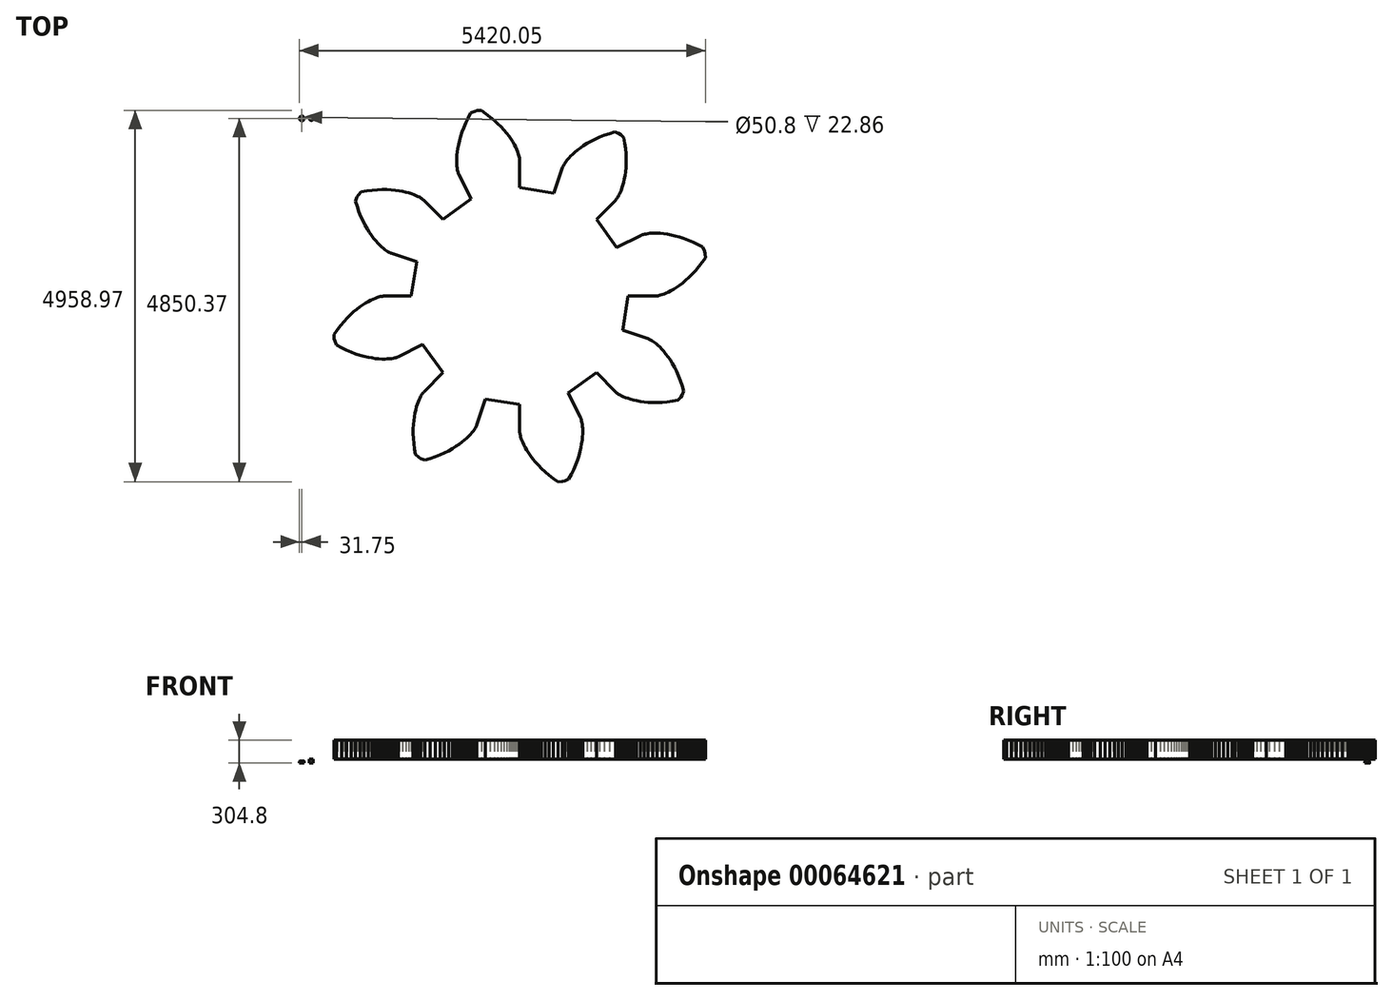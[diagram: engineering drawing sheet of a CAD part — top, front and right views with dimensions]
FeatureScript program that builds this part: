
annotation { "Feature Type Name" : "Feature", "Feature Type Description" : "" }
export const myFeature = defineFeature(function(context is Context, id is Id, definition is map)
    precondition{}
    {
        {
            var Q0;
            Q0=qCreatedBy(makeId("Top.planeOp"),FACE);
            var sketch = newSketch(context, id + "F0", { "sketchPlane" : qUnion([Q0])});
            skCircle(sketch, "E0", {"center": v(-25.4, 10.89) * mm, "radius": 25.4 * mm});
            skCircle(sketch, "E1", {"center": v(101.6, 10.89) * mm, "radius": 25.46 * mm});
            skCircle(sketch, "E2.0", {"center": v(-25.4, 10.89) * mm, "radius": 31.75 * mm});
            skSolve(sketch);
        }
        {
            var Q0;
            Q0=makeQuery(id+"F0.imprint","IMPRINT",FACE,{"disambiguationData":[TD([[makeQuery(id+"F0.imprint","IMPRINT",EDGE,{"derivedFrom":sQuery(id+"F0.wireOp",EDGE,"E0")}),-1.0]])]});
            extrude(context, id + "F1", {"entities" : qUnion([Q0]), "depth" : 25.4 * mm});
        }
        {
            var Q0;
            Q0=makeQuery(id+"F0.imprint","IMPRINT",FACE,{"disambiguationData":[TD([[makeQuery(id+"F0.imprint","IMPRINT",EDGE,{"derivedFrom":sQuery(id+"F0.wireOp",EDGE,"E1")}),1.0]])]});
            extrude(context, id + "F2", {"entities" : qUnion([Q0]), "depth" : 50.8 * mm});
        }
        {
            var Q0;
            Q0=makeQuery(id+"F1.opExtrude","CAP_EDGE",EDGE,{"disambiguationData":[OSD([sQuery(id+"F0.wireOp",EDGE,"E0")])],"isStart":false});
            fillet(context, id + "F3", {"entities" : qUnion([Q0]), "radius" : 2.54 * mm, "tangentPropagation" : true, "allowEdgeOverflow" : false});
        }
        {
            var Q0;
            Q0=makeQuery(id+"F1.opExtrude","CAP_EDGE",EDGE,{"disambiguationData":[OSD([sQuery(id+"F0.wireOp",EDGE,"E2.0")])],"isStart":false});
            chamfer(context, id + "F4", {"entities" : qUnion([Q0]), "width" : 5.08 * mm, "tangentPropagation" : true});
        }
        {
            var Q0;
            Q0=makeQuery(id+"F2.opExtrude","CAP_FACE",FACE,{"disambiguationData":[OSD([sQuery(id+"F0.wireOp",EDGE,"E1")])],"isStart":false});
            var sketch = newSketch(context, id + "F5", { "sketchPlane" : qUnion([Q0])});
            skLineSegment(sketch, "E3", {"start": v(4703.84, -2359.3) * mm, "end": v(4713.76, -2358.02) * mm});
            skLineSegment(sketch, "E4", {"start": v(4713.76, -2358.02) * mm, "end": v(4727, -2355.74) * mm});
            skLineSegment(sketch, "E5", {"start": v(4727, -2355.74) * mm, "end": v(4743.5, -2352.14) * mm});
            skLineSegment(sketch, "E6", {"start": v(4743.5, -2352.14) * mm, "end": v(4763.16, -2346.95) * mm});
            skLineSegment(sketch, "E7", {"start": v(4763.16, -2346.95) * mm, "end": v(4785.87, -2339.89) * mm});
            skLineSegment(sketch, "E8", {"start": v(4785.87, -2339.89) * mm, "end": v(4811.5, -2330.67) * mm});
            skLineSegment(sketch, "E9", {"start": v(4811.5, -2330.67) * mm, "end": v(4839.88, -2319.05) * mm});
            skLineSegment(sketch, "E10", {"start": v(4839.88, -2319.05) * mm, "end": v(4870.87, -2304.75) * mm});
            skLineSegment(sketch, "E11", {"start": v(4870.87, -2304.75) * mm, "end": v(4904.26, -2287.54) * mm});
            skLineSegment(sketch, "E12", {"start": v(4904.26, -2287.54) * mm, "end": v(4939.86, -2267.17) * mm});
            skLineSegment(sketch, "E13", {"start": v(4939.86, -2267.17) * mm, "end": v(4977.46, -2243.43) * mm});
            skLineSegment(sketch, "E14", {"start": v(4977.46, -2243.43) * mm, "end": v(5016.82, -2216.12) * mm});
            skLineSegment(sketch, "E15", {"start": v(5016.82, -2216.12) * mm, "end": v(5057.69, -2185.02) * mm});
            skLineSegment(sketch, "E16", {"start": v(5057.69, -2185.02) * mm, "end": v(5099.82, -2149.97) * mm});
            skLineSegment(sketch, "E17", {"start": v(5099.82, -2149.97) * mm, "end": v(5142.92, -2110.8) * mm});
            skLineSegment(sketch, "E18", {"start": v(5142.92, -2110.8) * mm, "end": v(5186.73, -2067.35) * mm});
            skLineSegment(sketch, "E19", {"start": v(5186.73, -2067.35) * mm, "end": v(5230.94, -2019.5) * mm});
            skLineSegment(sketch, "E20", {"start": v(5230.94, -2019.5) * mm, "end": v(5275.25, -1967.15) * mm});
            skLineSegment(sketch, "E21", {"start": v(5275.25, -1967.15) * mm, "end": v(5319.34, -1910.18) * mm});
            skLineSegment(sketch, "E22", {"start": v(5319.34, -1910.18) * mm, "end": v(5362.9, -1848.53) * mm});
            skLineSegment(sketch, "E23", {"start": v(5362.9, -1848.53) * mm, "end": v(5359.27, -1792.76) * mm});
            skLineSegment(sketch, "E24", {"start": v(5359.27, -1792.76) * mm, "end": v(5351.12, -1758.3) * mm});
            skLineSegment(sketch, "E25", {"start": v(5351.12, -1758.3) * mm, "end": v(5329.39, -1706.81) * mm});
            skLineSegment(sketch, "E26", {"start": v(5329.39, -1706.81) * mm, "end": v(5262.83, -1671.2) * mm});
            skLineSegment(sketch, "E27", {"start": v(5262.83, -1671.2) * mm, "end": v(5197.9, -1640.01) * mm});
            skLineSegment(sketch, "E28", {"start": v(5197.9, -1640.01) * mm, "end": v(5134.83, -1613.04) * mm});
            skLineSegment(sketch, "E29", {"start": v(5134.83, -1613.04) * mm, "end": v(5073.88, -1590.07) * mm});
            skLineSegment(sketch, "E30", {"start": v(5073.88, -1590.07) * mm, "end": v(5015.25, -1570.84) * mm});
            skLineSegment(sketch, "E31", {"start": v(5015.25, -1570.84) * mm, "end": v(4959.16, -1555.12) * mm});
            skLineSegment(sketch, "E32", {"start": v(4959.16, -1555.12) * mm, "end": v(4905.8, -1542.65) * mm});
            skLineSegment(sketch, "E33", {"start": v(4905.8, -1542.65) * mm, "end": v(4855.33, -1533.15) * mm});
            skLineSegment(sketch, "E34", {"start": v(4855.33, -1533.15) * mm, "end": v(4807.9, -1526.35) * mm});
            skLineSegment(sketch, "E35", {"start": v(4807.9, -1526.35) * mm, "end": v(4763.66, -1521.97) * mm});
            skLineSegment(sketch, "E36", {"start": v(4763.66, -1521.97) * mm, "end": v(4722.7, -1519.7) * mm});
            skLineSegment(sketch, "E37", {"start": v(4722.7, -1519.7) * mm, "end": v(4685.14, -1519.27) * mm});
            skLineSegment(sketch, "E38", {"start": v(4685.14, -1519.27) * mm, "end": v(4651.03, -1520.37) * mm});
            skLineSegment(sketch, "E39", {"start": v(4651.03, -1520.37) * mm, "end": v(4620.45, -1522.68) * mm});
            skLineSegment(sketch, "E40", {"start": v(4620.45, -1522.68) * mm, "end": v(4593.41, -1525.92) * mm});
            skLineSegment(sketch, "E41", {"start": v(4593.41, -1525.92) * mm, "end": v(4569.94, -1529.78) * mm});
            skLineSegment(sketch, "E42", {"start": v(4569.94, -1529.78) * mm, "end": v(4550.04, -1533.94) * mm});
            skLineSegment(sketch, "E43", {"start": v(4550.04, -1533.94) * mm, "end": v(4533.67, -1538.12) * mm});
            skLineSegment(sketch, "E44", {"start": v(4533.67, -1538.12) * mm, "end": v(4520.8, -1542) * mm});
            skLineSegment(sketch, "E45", {"start": v(4520.8, -1542) * mm, "end": v(4511.37, -1545.3) * mm});
            skLineSegment(sketch, "E46", {"start": v(4511.37, -1545.3) * mm, "end": v(4505.29, -1547.73) * mm});
            skLineSegment(sketch, "E47", {"start": v(4505.29, -1547.73) * mm, "end": v(4502.46, -1549) * mm});
            skLineSegment(sketch, "E48", {"start": v(4502.46, -1549) * mm, "end": v(4177.9, -1711.57) * mm});
            skLineSegment(sketch, "E49", {"start": v(4177.9, -1711.57) * mm, "end": v(3907.17, -1336.24) * mm});
            skLineSegment(sketch, "E50", {"start": v(3907.17, -1336.24) * mm, "end": v(4163.84, -1079.56) * mm});
            skLineSegment(sketch, "E51", {"start": v(4163.84, -1079.56) * mm, "end": v(4165.94, -1077.27) * mm});
            skLineSegment(sketch, "E52", {"start": v(4165.94, -1077.27) * mm, "end": v(4170.16, -1072.27) * mm});
            skLineSegment(sketch, "E53", {"start": v(4170.16, -1072.27) * mm, "end": v(4176.27, -1064.35) * mm});
            skLineSegment(sketch, "E54", {"start": v(4176.27, -1064.35) * mm, "end": v(4184.02, -1053.37) * mm});
            skLineSegment(sketch, "E55", {"start": v(4184.02, -1053.37) * mm, "end": v(4193.14, -1039.16) * mm});
            skLineSegment(sketch, "E56", {"start": v(4193.14, -1039.16) * mm, "end": v(4203.38, -1021.59) * mm});
            skLineSegment(sketch, "E57", {"start": v(4203.38, -1021.59) * mm, "end": v(4214.44, -1000.53) * mm});
            skLineSegment(sketch, "E58", {"start": v(4214.44, -1000.53) * mm, "end": v(4226.04, -975.9) * mm});
            skLineSegment(sketch, "E59", {"start": v(4226.04, -975.9) * mm, "end": v(4237.9, -947.6) * mm});
            skLineSegment(sketch, "E60", {"start": v(4237.9, -947.6) * mm, "end": v(4249.7, -915.59) * mm});
            skLineSegment(sketch, "E61", {"start": v(4249.7, -915.59) * mm, "end": v(4261.14, -879.8) * mm});
            skLineSegment(sketch, "E62", {"start": v(4261.14, -879.8) * mm, "end": v(4271.91, -840.23) * mm});
            skLineSegment(sketch, "E63", {"start": v(4271.91, -840.23) * mm, "end": v(4281.71, -796.86) * mm});
            skLineSegment(sketch, "E64", {"start": v(4281.71, -796.86) * mm, "end": v(4290.23, -749.71) * mm});
            skLineSegment(sketch, "E65", {"start": v(4290.23, -749.71) * mm, "end": v(4297.14, -698.82) * mm});
            skLineSegment(sketch, "E66", {"start": v(4297.14, -698.82) * mm, "end": v(4302.14, -644.25) * mm});
            skLineSegment(sketch, "E67", {"start": v(4302.14, -644.25) * mm, "end": v(4304.92, -586.07) * mm});
            skLineSegment(sketch, "E68", {"start": v(4304.92, -586.07) * mm, "end": v(4305.18, -524.37) * mm});
            skLineSegment(sketch, "E69", {"start": v(4305.18, -524.37) * mm, "end": v(4302.6, -459.28) * mm});
            skLineSegment(sketch, "E70", {"start": v(4302.6, -459.28) * mm, "end": v(4296.92, -390.93) * mm});
            skLineSegment(sketch, "E71", {"start": v(4296.92, -390.93) * mm, "end": v(4287.81, -319.47) * mm});
            skLineSegment(sketch, "E72", {"start": v(4287.81, -319.47) * mm, "end": v(4275.02, -245.08) * mm});
            skLineSegment(sketch, "E73", {"start": v(4275.02, -245.08) * mm, "end": v(4233.01, -208.2) * mm});
            skLineSegment(sketch, "E74", {"start": v(4233.01, -208.2) * mm, "end": v(4202.9, -189.6) * mm});
            skLineSegment(sketch, "E75", {"start": v(4202.9, -189.6) * mm, "end": v(4151.11, -168.56) * mm});
            skLineSegment(sketch, "E76", {"start": v(4151.11, -168.56) * mm, "end": v(4078.87, -190.44) * mm});
            skLineSegment(sketch, "E77", {"start": v(4078.87, -190.44) * mm, "end": v(4010.9, -214.3) * mm});
            skLineSegment(sketch, "E78", {"start": v(4010.9, -214.3) * mm, "end": v(3947.24, -239.83) * mm});
            skLineSegment(sketch, "E79", {"start": v(3947.24, -239.83) * mm, "end": v(3887.89, -266.68) * mm});
            skLineSegment(sketch, "E80", {"start": v(3887.89, -266.68) * mm, "end": v(3832.84, -294.54) * mm});
            skLineSegment(sketch, "E81", {"start": v(3832.84, -294.54) * mm, "end": v(3782.06, -323.09) * mm});
            skLineSegment(sketch, "E82", {"start": v(3782.06, -323.09) * mm, "end": v(3735.51, -352) * mm});
            skLineSegment(sketch, "E83", {"start": v(3735.51, -352) * mm, "end": v(3693.1, -380.97) * mm});
            skLineSegment(sketch, "E84", {"start": v(3693.1, -380.97) * mm, "end": v(3654.76, -409.7) * mm});
            skLineSegment(sketch, "E85", {"start": v(3654.76, -409.7) * mm, "end": v(3620.38, -437.89) * mm});
            skLineSegment(sketch, "E86", {"start": v(3620.38, -437.89) * mm, "end": v(3589.82, -465.25) * mm});
            skLineSegment(sketch, "E87", {"start": v(3589.82, -465.25) * mm, "end": v(3562.95, -491.5) * mm});
            skLineSegment(sketch, "E88", {"start": v(3562.95, -491.5) * mm, "end": v(3539.6, -516.4) * mm});
            skLineSegment(sketch, "E89", {"start": v(3539.6, -516.4) * mm, "end": v(3519.62, -539.66) * mm});
            skLineSegment(sketch, "E90", {"start": v(3519.62, -539.66) * mm, "end": v(3502.79, -561.07) * mm});
            skLineSegment(sketch, "E91", {"start": v(3502.79, -561.07) * mm, "end": v(3488.92, -580.39) * mm});
            skLineSegment(sketch, "E92", {"start": v(3488.92, -580.39) * mm, "end": v(3477.8, -597.4) * mm});
            skLineSegment(sketch, "E93", {"start": v(3477.8, -597.4) * mm, "end": v(3469.17, -611.93) * mm});
            skLineSegment(sketch, "E94", {"start": v(3469.17, -611.93) * mm, "end": v(3462.82, -623.78) * mm});
            skLineSegment(sketch, "E95", {"start": v(3462.82, -623.78) * mm, "end": v(3458.48, -632.78) * mm});
            skLineSegment(sketch, "E96", {"start": v(3458.48, -632.78) * mm, "end": v(3455.9, -638.8) * mm});
            skLineSegment(sketch, "E97", {"start": v(3455.9, -638.8) * mm, "end": v(3454.8, -641.7) * mm});
            skLineSegment(sketch, "E98", {"start": v(3454.8, -641.7) * mm, "end": v(3340.25, -986.15) * mm});
            skLineSegment(sketch, "E99", {"start": v(3340.25, -986.15) * mm, "end": v(2883.42, -912.2) * mm});
            skLineSegment(sketch, "E100", {"start": v(2883.42, -912.2) * mm, "end": v(2883.41, -549.19) * mm});
            skLineSegment(sketch, "E101", {"start": v(2883.41, -549.19) * mm, "end": v(2883.27, -546.1) * mm});
            skLineSegment(sketch, "E102", {"start": v(2883.27, -546.1) * mm, "end": v(2882.71, -539.56) * mm});
            skLineSegment(sketch, "E103", {"start": v(2882.71, -539.56) * mm, "end": v(2881.44, -529.65) * mm});
            skLineSegment(sketch, "E104", {"start": v(2881.44, -529.65) * mm, "end": v(2879.15, -516.4) * mm});
            skLineSegment(sketch, "E105", {"start": v(2879.15, -516.4) * mm, "end": v(2875.56, -499.9) * mm});
            skLineSegment(sketch, "E106", {"start": v(2875.56, -499.9) * mm, "end": v(2870.37, -480.24) * mm});
            skLineSegment(sketch, "E107", {"start": v(2870.37, -480.24) * mm, "end": v(2863.3, -457.53) * mm});
            skLineSegment(sketch, "E108", {"start": v(2863.3, -457.53) * mm, "end": v(2854.09, -431.9) * mm});
            skLineSegment(sketch, "E109", {"start": v(2854.09, -431.9) * mm, "end": v(2842.46, -403.52) * mm});
            skLineSegment(sketch, "E110", {"start": v(2842.46, -403.52) * mm, "end": v(2828.17, -372.54) * mm});
            skLineSegment(sketch, "E111", {"start": v(2828.17, -372.54) * mm, "end": v(2810.95, -339.15) * mm});
            skLineSegment(sketch, "E112", {"start": v(2810.95, -339.15) * mm, "end": v(2790.59, -303.54) * mm});
            skLineSegment(sketch, "E113", {"start": v(2790.59, -303.54) * mm, "end": v(2766.85, -265.95) * mm});
            skLineSegment(sketch, "E114", {"start": v(2766.85, -265.95) * mm, "end": v(2739.53, -226.59) * mm});
            skLineSegment(sketch, "E115", {"start": v(2739.53, -226.59) * mm, "end": v(2708.44, -185.72) * mm});
            skLineSegment(sketch, "E116", {"start": v(2708.44, -185.72) * mm, "end": v(2673.39, -143.6) * mm});
            skLineSegment(sketch, "E117", {"start": v(2673.39, -143.6) * mm, "end": v(2634.21, -100.48) * mm});
            skLineSegment(sketch, "E118", {"start": v(2634.21, -100.48) * mm, "end": v(2590.77, -56.67) * mm});
            skLineSegment(sketch, "E119", {"start": v(2590.77, -56.67) * mm, "end": v(2542.92, -12.46) * mm});
            skLineSegment(sketch, "E120", {"start": v(2542.92, -12.46) * mm, "end": v(2490.56, 31.84) * mm});
            skLineSegment(sketch, "E121", {"start": v(2490.56, 31.84) * mm, "end": v(2433.6, 75.94) * mm});
            skLineSegment(sketch, "E122", {"start": v(2433.6, 75.94) * mm, "end": v(2371.95, 119.5) * mm});
            skLineSegment(sketch, "E123", {"start": v(2371.95, 119.5) * mm, "end": v(2316.17, 115.86) * mm});
            skLineSegment(sketch, "E124", {"start": v(2316.17, 115.86) * mm, "end": v(2281.73, 107.72) * mm});
            skLineSegment(sketch, "E125", {"start": v(2281.73, 107.72) * mm, "end": v(2230.23, 85.98) * mm});
            skLineSegment(sketch, "E126", {"start": v(2230.23, 85.98) * mm, "end": v(2194.62, 19.43) * mm});
            skLineSegment(sketch, "E127", {"start": v(2194.62, 19.43) * mm, "end": v(2163.43, -45.5) * mm});
            skLineSegment(sketch, "E128", {"start": v(2163.43, -45.5) * mm, "end": v(2136.46, -108.57) * mm});
            skLineSegment(sketch, "E129", {"start": v(2136.46, -108.57) * mm, "end": v(2113.48, -169.53) * mm});
            skLineSegment(sketch, "E130", {"start": v(2113.48, -169.53) * mm, "end": v(2094.26, -228.15) * mm});
            skLineSegment(sketch, "E131", {"start": v(2094.26, -228.15) * mm, "end": v(2078.54, -284.24) * mm});
            skLineSegment(sketch, "E132", {"start": v(2078.54, -284.24) * mm, "end": v(2066.07, -337.6) * mm});
            skLineSegment(sketch, "E133", {"start": v(2066.07, -337.6) * mm, "end": v(2056.57, -388.08) * mm});
            skLineSegment(sketch, "E134", {"start": v(2056.57, -388.08) * mm, "end": v(2049.77, -435.5) * mm});
            skLineSegment(sketch, "E135", {"start": v(2049.77, -435.5) * mm, "end": v(2045.39, -479.75) * mm});
            skLineSegment(sketch, "E136", {"start": v(2045.39, -479.75) * mm, "end": v(2043.12, -520.7) * mm});
            skLineSegment(sketch, "E137", {"start": v(2043.12, -520.7) * mm, "end": v(2042.69, -558.27) * mm});
            skLineSegment(sketch, "E138", {"start": v(2042.69, -558.27) * mm, "end": v(2043.78, -592.37) * mm});
            skLineSegment(sketch, "E139", {"start": v(2043.78, -592.37) * mm, "end": v(2046.1, -622.96) * mm});
            skLineSegment(sketch, "E140", {"start": v(2046.1, -622.96) * mm, "end": v(2049.34, -650) * mm});
            skLineSegment(sketch, "E141", {"start": v(2049.34, -650) * mm, "end": v(2053.2, -673.46) * mm});
            skLineSegment(sketch, "E142", {"start": v(2053.2, -673.46) * mm, "end": v(2057.36, -693.37) * mm});
            skLineSegment(sketch, "E143", {"start": v(2057.36, -693.37) * mm, "end": v(2061.53, -709.73) * mm});
            skLineSegment(sketch, "E144", {"start": v(2061.53, -709.73) * mm, "end": v(2065.42, -722.6) * mm});
            skLineSegment(sketch, "E145", {"start": v(2065.42, -722.6) * mm, "end": v(2068.72, -732.04) * mm});
            skLineSegment(sketch, "E146", {"start": v(2068.72, -732.04) * mm, "end": v(2071.15, -738.12) * mm});
            skLineSegment(sketch, "E147", {"start": v(2071.15, -738.12) * mm, "end": v(2072.42, -740.95) * mm});
            skLineSegment(sketch, "E148", {"start": v(2072.42, -740.95) * mm, "end": v(2234.99, -1065.51) * mm});
            skLineSegment(sketch, "E149", {"start": v(2234.99, -1065.51) * mm, "end": v(1859.66, -1336.24) * mm});
            skLineSegment(sketch, "E150", {"start": v(1859.66, -1336.24) * mm, "end": v(1602.97, -1079.56) * mm});
            skLineSegment(sketch, "E151", {"start": v(1602.97, -1079.56) * mm, "end": v(1600.69, -1077.47) * mm});
            skLineSegment(sketch, "E152", {"start": v(1600.69, -1077.47) * mm, "end": v(1595.68, -1073.24) * mm});
            skLineSegment(sketch, "E153", {"start": v(1595.68, -1073.24) * mm, "end": v(1587.77, -1067.13) * mm});
            skLineSegment(sketch, "E154", {"start": v(1587.77, -1067.13) * mm, "end": v(1576.79, -1059.39) * mm});
            skLineSegment(sketch, "E155", {"start": v(1576.79, -1059.39) * mm, "end": v(1562.58, -1050.26) * mm});
            skLineSegment(sketch, "E156", {"start": v(1562.58, -1050.26) * mm, "end": v(1545, -1040.03) * mm});
            skLineSegment(sketch, "E157", {"start": v(1545, -1040.03) * mm, "end": v(1523.95, -1028.97) * mm});
            skLineSegment(sketch, "E158", {"start": v(1523.95, -1028.97) * mm, "end": v(1499.32, -1017.36) * mm});
            skLineSegment(sketch, "E159", {"start": v(1499.32, -1017.36) * mm, "end": v(1471.02, -1005.51) * mm});
            skLineSegment(sketch, "E160", {"start": v(1471.02, -1005.51) * mm, "end": v(1439, -993.71) * mm});
            skLineSegment(sketch, "E161", {"start": v(1439, -993.71) * mm, "end": v(1403.22, -982.27) * mm});
            skLineSegment(sketch, "E162", {"start": v(1403.22, -982.27) * mm, "end": v(1363.65, -971.5) * mm});
            skLineSegment(sketch, "E163", {"start": v(1363.65, -971.5) * mm, "end": v(1320.28, -961.7) * mm});
            skLineSegment(sketch, "E164", {"start": v(1320.28, -961.7) * mm, "end": v(1273.13, -953.18) * mm});
            skLineSegment(sketch, "E165", {"start": v(1273.13, -953.18) * mm, "end": v(1222.24, -946.27) * mm});
            skLineSegment(sketch, "E166", {"start": v(1222.24, -946.27) * mm, "end": v(1167.67, -941.27) * mm});
            skLineSegment(sketch, "E167", {"start": v(1167.67, -941.27) * mm, "end": v(1109.49, -938.48) * mm});
            skLineSegment(sketch, "E168", {"start": v(1109.49, -938.48) * mm, "end": v(1047.79, -938.23) * mm});
            skLineSegment(sketch, "E169", {"start": v(1047.79, -938.23) * mm, "end": v(982.7, -940.8) * mm});
            skLineSegment(sketch, "E170", {"start": v(982.7, -940.8) * mm, "end": v(914.34, -946.49) * mm});
            skLineSegment(sketch, "E171", {"start": v(914.34, -946.49) * mm, "end": v(842.88, -955.6) * mm});
            skLineSegment(sketch, "E172", {"start": v(842.88, -955.6) * mm, "end": v(768.5, -968.39) * mm});
            skLineSegment(sketch, "E173", {"start": v(768.5, -968.39) * mm, "end": v(731.62, -1010.4) * mm});
            skLineSegment(sketch, "E174", {"start": v(731.62, -1010.4) * mm, "end": v(713.02, -1040.5) * mm});
            skLineSegment(sketch, "E175", {"start": v(713.02, -1040.5) * mm, "end": v(691.98, -1092.3) * mm});
            skLineSegment(sketch, "E176", {"start": v(691.98, -1092.3) * mm, "end": v(713.85, -1164.54) * mm});
            skLineSegment(sketch, "E177", {"start": v(713.85, -1164.54) * mm, "end": v(737.72, -1232.5) * mm});
            skLineSegment(sketch, "E178", {"start": v(737.72, -1232.5) * mm, "end": v(763.24, -1296.17) * mm});
            skLineSegment(sketch, "E179", {"start": v(763.24, -1296.17) * mm, "end": v(790.1, -1355.52) * mm});
            skLineSegment(sketch, "E180", {"start": v(790.1, -1355.52) * mm, "end": v(817.96, -1410.57) * mm});
            skLineSegment(sketch, "E181", {"start": v(817.96, -1410.57) * mm, "end": v(846.5, -1461.34) * mm});
            skLineSegment(sketch, "E182", {"start": v(846.5, -1461.34) * mm, "end": v(875.42, -1507.9) * mm});
            skLineSegment(sketch, "E183", {"start": v(875.42, -1507.9) * mm, "end": v(904.4, -1550.3) * mm});
            skLineSegment(sketch, "E184", {"start": v(904.4, -1550.3) * mm, "end": v(933.12, -1588.64) * mm});
            skLineSegment(sketch, "E185", {"start": v(933.12, -1588.64) * mm, "end": v(961.3, -1623.03) * mm});
            skLineSegment(sketch, "E186", {"start": v(961.3, -1623.03) * mm, "end": v(988.66, -1653.59) * mm});
            skLineSegment(sketch, "E187", {"start": v(988.66, -1653.59) * mm, "end": v(1014.92, -1680.46) * mm});
            skLineSegment(sketch, "E188", {"start": v(1014.92, -1680.46) * mm, "end": v(1039.8, -1703.8) * mm});
            skLineSegment(sketch, "E189", {"start": v(1039.8, -1703.8) * mm, "end": v(1063.08, -1723.79) * mm});
            skLineSegment(sketch, "E190", {"start": v(1063.08, -1723.79) * mm, "end": v(1084.48, -1740.62) * mm});
            skLineSegment(sketch, "E191", {"start": v(1084.48, -1740.62) * mm, "end": v(1103.8, -1754.49) * mm});
            skLineSegment(sketch, "E192", {"start": v(1103.8, -1754.49) * mm, "end": v(1120.82, -1765.61) * mm});
            skLineSegment(sketch, "E193", {"start": v(1120.82, -1765.61) * mm, "end": v(1135.35, -1774.23) * mm});
            skLineSegment(sketch, "E194", {"start": v(1135.35, -1774.23) * mm, "end": v(1147.2, -1780.59) * mm});
            skLineSegment(sketch, "E195", {"start": v(1147.2, -1780.59) * mm, "end": v(1156.2, -1784.92) * mm});
            skLineSegment(sketch, "E196", {"start": v(1156.2, -1784.92) * mm, "end": v(1162.22, -1787.5) * mm});
            skLineSegment(sketch, "E197", {"start": v(1162.22, -1787.5) * mm, "end": v(1165.12, -1788.61) * mm});
            skLineSegment(sketch, "E198", {"start": v(1165.12, -1788.61) * mm, "end": v(1509.57, -1903.16) * mm});
            skLineSegment(sketch, "E199", {"start": v(1509.57, -1903.16) * mm, "end": v(1435.6, -2360) * mm});
            skLineSegment(sketch, "E200", {"start": v(1435.6, -2360) * mm, "end": v(1072.6, -2360) * mm});
            skLineSegment(sketch, "E201", {"start": v(1072.6, -2360) * mm, "end": v(1069.5, -2360.14) * mm});
            skLineSegment(sketch, "E202", {"start": v(1069.5, -2360.14) * mm, "end": v(1062.98, -2360.7) * mm});
            skLineSegment(sketch, "E203", {"start": v(1062.98, -2360.7) * mm, "end": v(1053.07, -2361.97) * mm});
            skLineSegment(sketch, "E204", {"start": v(1053.07, -2361.97) * mm, "end": v(1039.82, -2364.25) * mm});
            skLineSegment(sketch, "E205", {"start": v(1039.82, -2364.25) * mm, "end": v(1023.32, -2367.85) * mm});
            skLineSegment(sketch, "E206", {"start": v(1023.32, -2367.85) * mm, "end": v(1003.66, -2373.04) * mm});
            skLineSegment(sketch, "E207", {"start": v(1003.66, -2373.04) * mm, "end": v(980.95, -2380.1) * mm});
            skLineSegment(sketch, "E208", {"start": v(980.95, -2380.1) * mm, "end": v(955.33, -2389.32) * mm});
            skLineSegment(sketch, "E209", {"start": v(955.33, -2389.32) * mm, "end": v(926.94, -2400.94) * mm});
            skLineSegment(sketch, "E210", {"start": v(926.94, -2400.94) * mm, "end": v(895.96, -2415.24) * mm});
            skLineSegment(sketch, "E211", {"start": v(895.96, -2415.24) * mm, "end": v(862.56, -2432.45) * mm});
            skLineSegment(sketch, "E212", {"start": v(862.56, -2432.45) * mm, "end": v(826.96, -2452.82) * mm});
            skLineSegment(sketch, "E213", {"start": v(826.96, -2452.82) * mm, "end": v(789.36, -2476.55) * mm});
            skLineSegment(sketch, "E214", {"start": v(789.36, -2476.55) * mm, "end": v(750, -2503.87) * mm});
            skLineSegment(sketch, "E215", {"start": v(750, -2503.87) * mm, "end": v(709.13, -2534.97) * mm});
            skLineSegment(sketch, "E216", {"start": v(709.13, -2534.97) * mm, "end": v(667, -2570.02) * mm});
            skLineSegment(sketch, "E217", {"start": v(667, -2570.02) * mm, "end": v(623.9, -2609.2) * mm});
            skLineSegment(sketch, "E218", {"start": v(623.9, -2609.2) * mm, "end": v(580.1, -2652.64) * mm});
            skLineSegment(sketch, "E219", {"start": v(580.1, -2652.64) * mm, "end": v(535.88, -2700.48) * mm});
            skLineSegment(sketch, "E220", {"start": v(535.88, -2700.48) * mm, "end": v(491.57, -2752.84) * mm});
            skLineSegment(sketch, "E221", {"start": v(491.57, -2752.84) * mm, "end": v(447.48, -2809.8) * mm});
            skLineSegment(sketch, "E222", {"start": v(447.48, -2809.8) * mm, "end": v(403.93, -2871.46) * mm});
            skLineSegment(sketch, "E223", {"start": v(403.93, -2871.46) * mm, "end": v(407.56, -2927.23) * mm});
            skLineSegment(sketch, "E224", {"start": v(407.56, -2927.23) * mm, "end": v(415.7, -2961.68) * mm});
            skLineSegment(sketch, "E225", {"start": v(415.7, -2961.68) * mm, "end": v(437.44, -3013.17) * mm});
            skLineSegment(sketch, "E226", {"start": v(437.44, -3013.17) * mm, "end": v(503.99, -3048.79) * mm});
            skLineSegment(sketch, "E227", {"start": v(503.99, -3048.79) * mm, "end": v(568.92, -3079.98) * mm});
            skLineSegment(sketch, "E228", {"start": v(568.92, -3079.98) * mm, "end": v(631.99, -3106.95) * mm});
            skLineSegment(sketch, "E229", {"start": v(631.99, -3106.95) * mm, "end": v(692.95, -3129.92) * mm});
            skLineSegment(sketch, "E230", {"start": v(692.95, -3129.92) * mm, "end": v(751.57, -3149.15) * mm});
            skLineSegment(sketch, "E231", {"start": v(751.57, -3149.15) * mm, "end": v(807.66, -3164.87) * mm});
            skLineSegment(sketch, "E232", {"start": v(807.66, -3164.87) * mm, "end": v(861.02, -3177.34) * mm});
            skLineSegment(sketch, "E233", {"start": v(861.02, -3177.34) * mm, "end": v(911.5, -3186.84) * mm});
            skLineSegment(sketch, "E234", {"start": v(911.5, -3186.84) * mm, "end": v(958.92, -3193.63) * mm});
            skLineSegment(sketch, "E235", {"start": v(958.92, -3193.63) * mm, "end": v(1003.16, -3198.02) * mm});
            skLineSegment(sketch, "E236", {"start": v(1003.16, -3198.02) * mm, "end": v(1044.12, -3200.28) * mm});
            skLineSegment(sketch, "E237", {"start": v(1044.12, -3200.28) * mm, "end": v(1081.68, -3200.72) * mm});
            skLineSegment(sketch, "E238", {"start": v(1081.68, -3200.72) * mm, "end": v(1115.79, -3199.62) * mm});
            skLineSegment(sketch, "E239", {"start": v(1115.79, -3199.62) * mm, "end": v(1146.38, -3197.3) * mm});
            skLineSegment(sketch, "E240", {"start": v(1146.38, -3197.3) * mm, "end": v(1173.41, -3194.07) * mm});
            skLineSegment(sketch, "E241", {"start": v(1173.41, -3194.07) * mm, "end": v(1196.88, -3190.21) * mm});
            skLineSegment(sketch, "E242", {"start": v(1196.88, -3190.21) * mm, "end": v(1216.79, -3186.05) * mm});
            skLineSegment(sketch, "E243", {"start": v(1216.79, -3186.05) * mm, "end": v(1233.15, -3181.87) * mm});
            skLineSegment(sketch, "E244", {"start": v(1233.15, -3181.87) * mm, "end": v(1246.02, -3177.98) * mm});
            skLineSegment(sketch, "E245", {"start": v(1246.02, -3177.98) * mm, "end": v(1255.45, -3174.68) * mm});
            skLineSegment(sketch, "E246", {"start": v(1255.45, -3174.68) * mm, "end": v(1261.54, -3172.26) * mm});
            skLineSegment(sketch, "E247", {"start": v(1261.54, -3172.26) * mm, "end": v(1264.37, -3171) * mm});
            skLineSegment(sketch, "E248", {"start": v(1264.37, -3171) * mm, "end": v(1588.93, -3008.42) * mm});
            skLineSegment(sketch, "E249", {"start": v(1588.93, -3008.42) * mm, "end": v(1859.66, -3383.75) * mm});
            skLineSegment(sketch, "E250", {"start": v(1859.66, -3383.75) * mm, "end": v(1602.98, -3640.43) * mm});
            skLineSegment(sketch, "E251", {"start": v(1602.98, -3640.43) * mm, "end": v(1600.88, -3642.72) * mm});
            skLineSegment(sketch, "E252", {"start": v(1600.88, -3642.72) * mm, "end": v(1596.66, -3647.72) * mm});
            skLineSegment(sketch, "E253", {"start": v(1596.66, -3647.72) * mm, "end": v(1590.55, -3655.63) * mm});
            skLineSegment(sketch, "E254", {"start": v(1590.55, -3655.63) * mm, "end": v(1582.8, -3666.62) * mm});
            skLineSegment(sketch, "E255", {"start": v(1582.8, -3666.62) * mm, "end": v(1573.68, -3680.83) * mm});
            skLineSegment(sketch, "E256", {"start": v(1573.68, -3680.83) * mm, "end": v(1563.44, -3698.4) * mm});
            skLineSegment(sketch, "E257", {"start": v(1563.44, -3698.4) * mm, "end": v(1552.38, -3719.46) * mm});
            skLineSegment(sketch, "E258", {"start": v(1552.38, -3719.46) * mm, "end": v(1540.78, -3744.09) * mm});
            skLineSegment(sketch, "E259", {"start": v(1540.78, -3744.09) * mm, "end": v(1528.93, -3772.38) * mm});
            skLineSegment(sketch, "E260", {"start": v(1528.93, -3772.38) * mm, "end": v(1517.13, -3804.4) * mm});
            skLineSegment(sketch, "E261", {"start": v(1517.13, -3804.4) * mm, "end": v(1505.69, -3840.18) * mm});
            skLineSegment(sketch, "E262", {"start": v(1505.69, -3840.18) * mm, "end": v(1494.91, -3879.76) * mm});
            skLineSegment(sketch, "E263", {"start": v(1494.91, -3879.76) * mm, "end": v(1485.11, -3923.13) * mm});
            skLineSegment(sketch, "E264", {"start": v(1485.11, -3923.13) * mm, "end": v(1476.6, -3970.28) * mm});
            skLineSegment(sketch, "E265", {"start": v(1476.6, -3970.28) * mm, "end": v(1469.68, -4021.16) * mm});
            skLineSegment(sketch, "E266", {"start": v(1469.68, -4021.16) * mm, "end": v(1464.68, -4075.74) * mm});
            skLineSegment(sketch, "E267", {"start": v(1464.68, -4075.74) * mm, "end": v(1461.9, -4133.92) * mm});
            skLineSegment(sketch, "E268", {"start": v(1461.9, -4133.92) * mm, "end": v(1461.64, -4195.62) * mm});
            skLineSegment(sketch, "E269", {"start": v(1461.64, -4195.62) * mm, "end": v(1464.21, -4260.7) * mm});
            skLineSegment(sketch, "E270", {"start": v(1464.21, -4260.7) * mm, "end": v(1469.9, -4329.06) * mm});
            skLineSegment(sketch, "E271", {"start": v(1469.9, -4329.06) * mm, "end": v(1479, -4400.52) * mm});
            skLineSegment(sketch, "E272", {"start": v(1479, -4400.52) * mm, "end": v(1491.8, -4474.91) * mm});
            skLineSegment(sketch, "E273", {"start": v(1491.8, -4474.91) * mm, "end": v(1533.81, -4511.79) * mm});
            skLineSegment(sketch, "E274", {"start": v(1533.81, -4511.79) * mm, "end": v(1563.93, -4530.38) * mm});
            skLineSegment(sketch, "E275", {"start": v(1563.93, -4530.38) * mm, "end": v(1615.71, -4551.43) * mm});
            skLineSegment(sketch, "E276", {"start": v(1615.71, -4551.43) * mm, "end": v(1687.95, -4529.55) * mm});
            skLineSegment(sketch, "E277", {"start": v(1687.95, -4529.55) * mm, "end": v(1755.92, -4505.68) * mm});
            skLineSegment(sketch, "E278", {"start": v(1755.92, -4505.68) * mm, "end": v(1819.59, -4480.16) * mm});
            skLineSegment(sketch, "E279", {"start": v(1819.59, -4480.16) * mm, "end": v(1878.94, -4453.3) * mm});
            skLineSegment(sketch, "E280", {"start": v(1878.94, -4453.3) * mm, "end": v(1933.98, -4425.45) * mm});
            skLineSegment(sketch, "E281", {"start": v(1933.98, -4425.45) * mm, "end": v(1984.76, -4396.9) * mm});
            skLineSegment(sketch, "E282", {"start": v(1984.76, -4396.9) * mm, "end": v(2031.31, -4367.99) * mm});
            skLineSegment(sketch, "E283", {"start": v(2031.31, -4367.99) * mm, "end": v(2073.72, -4339.01) * mm});
            skLineSegment(sketch, "E284", {"start": v(2073.72, -4339.01) * mm, "end": v(2112.06, -4310.29) * mm});
            skLineSegment(sketch, "E285", {"start": v(2112.06, -4310.29) * mm, "end": v(2146.45, -4282.1) * mm});
            skLineSegment(sketch, "E286", {"start": v(2146.45, -4282.1) * mm, "end": v(2177, -4254.74) * mm});
            skLineSegment(sketch, "E287", {"start": v(2177, -4254.74) * mm, "end": v(2203.87, -4228.49) * mm});
            skLineSegment(sketch, "E288", {"start": v(2203.87, -4228.49) * mm, "end": v(2227.22, -4203.6) * mm});
            skLineSegment(sketch, "E289", {"start": v(2227.22, -4203.6) * mm, "end": v(2247.2, -4180.33) * mm});
            skLineSegment(sketch, "E290", {"start": v(2247.2, -4180.33) * mm, "end": v(2264.03, -4158.92) * mm});
            skLineSegment(sketch, "E291", {"start": v(2264.03, -4158.92) * mm, "end": v(2277.9, -4139.6) * mm});
            skLineSegment(sketch, "E292", {"start": v(2277.9, -4139.6) * mm, "end": v(2289.03, -4122.58) * mm});
            skLineSegment(sketch, "E293", {"start": v(2289.03, -4122.58) * mm, "end": v(2297.65, -4108.06) * mm});
            skLineSegment(sketch, "E294", {"start": v(2297.65, -4108.06) * mm, "end": v(2304, -4096.21) * mm});
            skLineSegment(sketch, "E295", {"start": v(2304, -4096.21) * mm, "end": v(2308.34, -4087.2) * mm});
            skLineSegment(sketch, "E296", {"start": v(2308.34, -4087.2) * mm, "end": v(2310.92, -4081.2) * mm});
            skLineSegment(sketch, "E297", {"start": v(2310.92, -4081.2) * mm, "end": v(2312.03, -4078.3) * mm});
            skLineSegment(sketch, "E298", {"start": v(2312.03, -4078.3) * mm, "end": v(2426.57, -3733.84) * mm});
            skLineSegment(sketch, "E299", {"start": v(2426.57, -3733.84) * mm, "end": v(2883.4, -3807.8) * mm});
            skLineSegment(sketch, "E300", {"start": v(2883.4, -3807.8) * mm, "end": v(2883.41, -4170.8) * mm});
            skLineSegment(sketch, "E301", {"start": v(2883.41, -4170.8) * mm, "end": v(2883.55, -4173.9) * mm});
            skLineSegment(sketch, "E302", {"start": v(2883.55, -4173.9) * mm, "end": v(2884.1, -4180.42) * mm});
            skLineSegment(sketch, "E303", {"start": v(2884.1, -4180.42) * mm, "end": v(2885.38, -4190.34) * mm});
            skLineSegment(sketch, "E304", {"start": v(2885.38, -4190.34) * mm, "end": v(2887.67, -4203.58) * mm});
            skLineSegment(sketch, "E305", {"start": v(2887.67, -4203.58) * mm, "end": v(2891.26, -4220.09) * mm});
            skLineSegment(sketch, "E306", {"start": v(2891.26, -4220.09) * mm, "end": v(2896.45, -4239.75) * mm});
            skLineSegment(sketch, "E307", {"start": v(2896.45, -4239.75) * mm, "end": v(2903.52, -4262.46) * mm});
            skLineSegment(sketch, "E308", {"start": v(2903.52, -4262.46) * mm, "end": v(2912.73, -4288.08) * mm});
            skLineSegment(sketch, "E309", {"start": v(2912.73, -4288.08) * mm, "end": v(2924.36, -4316.47) * mm});
            skLineSegment(sketch, "E310", {"start": v(2924.36, -4316.47) * mm, "end": v(2938.66, -4347.45) * mm});
            skLineSegment(sketch, "E311", {"start": v(2938.66, -4347.45) * mm, "end": v(2955.87, -4380.84) * mm});
            skLineSegment(sketch, "E312", {"start": v(2955.87, -4380.84) * mm, "end": v(2976.23, -4416.45) * mm});
            skLineSegment(sketch, "E313", {"start": v(2976.23, -4416.45) * mm, "end": v(2999.97, -4454.04) * mm});
            skLineSegment(sketch, "E314", {"start": v(2999.97, -4454.04) * mm, "end": v(3027.29, -4493.4) * mm});
            skLineSegment(sketch, "E315", {"start": v(3027.29, -4493.4) * mm, "end": v(3058.38, -4534.27) * mm});
            skLineSegment(sketch, "E316", {"start": v(3058.38, -4534.27) * mm, "end": v(3093.44, -4576.4) * mm});
            skLineSegment(sketch, "E317", {"start": v(3093.44, -4576.4) * mm, "end": v(3132.61, -4619.5) * mm});
            skLineSegment(sketch, "E318", {"start": v(3132.61, -4619.5) * mm, "end": v(3176.05, -4663.32) * mm});
            skLineSegment(sketch, "E319", {"start": v(3176.05, -4663.32) * mm, "end": v(3223.9, -4707.53) * mm});
            skLineSegment(sketch, "E320", {"start": v(3223.9, -4707.53) * mm, "end": v(3276.26, -4751.83) * mm});
            skLineSegment(sketch, "E321", {"start": v(3276.26, -4751.83) * mm, "end": v(3333.22, -4795.93) * mm});
            skLineSegment(sketch, "E322", {"start": v(3333.22, -4795.93) * mm, "end": v(3394.87, -4839.48) * mm});
            skLineSegment(sketch, "E323", {"start": v(3394.87, -4839.48) * mm, "end": v(3450.65, -4835.85) * mm});
            skLineSegment(sketch, "E324", {"start": v(3450.65, -4835.85) * mm, "end": v(3485.1, -4827.7) * mm});
            skLineSegment(sketch, "E325", {"start": v(3485.1, -4827.7) * mm, "end": v(3536.6, -4805.97) * mm});
            skLineSegment(sketch, "E326", {"start": v(3536.6, -4805.97) * mm, "end": v(3572.2, -4739.42) * mm});
            skLineSegment(sketch, "E327", {"start": v(3572.2, -4739.42) * mm, "end": v(3603.4, -4674.48) * mm});
            skLineSegment(sketch, "E328", {"start": v(3603.4, -4674.48) * mm, "end": v(3630.36, -4611.42) * mm});
            skLineSegment(sketch, "E329", {"start": v(3630.36, -4611.42) * mm, "end": v(3653.34, -4550.46) * mm});
            skLineSegment(sketch, "E330", {"start": v(3653.34, -4550.46) * mm, "end": v(3672.56, -4491.83) * mm});
            skLineSegment(sketch, "E331", {"start": v(3672.56, -4491.83) * mm, "end": v(3688.28, -4435.75) * mm});
            skLineSegment(sketch, "E332", {"start": v(3688.28, -4435.75) * mm, "end": v(3700.76, -4382.38) * mm});
            skLineSegment(sketch, "E333", {"start": v(3700.76, -4382.38) * mm, "end": v(3710.25, -4331.91) * mm});
            skLineSegment(sketch, "E334", {"start": v(3710.25, -4331.91) * mm, "end": v(3717.05, -4284.49) * mm});
            skLineSegment(sketch, "E335", {"start": v(3717.05, -4284.49) * mm, "end": v(3721.44, -4240.24) * mm});
            skLineSegment(sketch, "E336", {"start": v(3721.44, -4240.24) * mm, "end": v(3723.7, -4199.29) * mm});
            skLineSegment(sketch, "E337", {"start": v(3723.7, -4199.29) * mm, "end": v(3724.13, -4161.72) * mm});
            skLineSegment(sketch, "E338", {"start": v(3724.13, -4161.72) * mm, "end": v(3723.04, -4127.62) * mm});
            skLineSegment(sketch, "E339", {"start": v(3723.04, -4127.62) * mm, "end": v(3720.72, -4097.03) * mm});
            skLineSegment(sketch, "E340", {"start": v(3720.72, -4097.03) * mm, "end": v(3717.48, -4070) * mm});
            skLineSegment(sketch, "E341", {"start": v(3717.48, -4070) * mm, "end": v(3713.63, -4046.53) * mm});
            skLineSegment(sketch, "E342", {"start": v(3713.63, -4046.53) * mm, "end": v(3709.46, -4026.62) * mm});
            skLineSegment(sketch, "E343", {"start": v(3709.46, -4026.62) * mm, "end": v(3705.29, -4010.26) * mm});
            skLineSegment(sketch, "E344", {"start": v(3705.29, -4010.26) * mm, "end": v(3701.4, -3997.39) * mm});
            skLineSegment(sketch, "E345", {"start": v(3701.4, -3997.39) * mm, "end": v(3698.1, -3987.95) * mm});
            skLineSegment(sketch, "E346", {"start": v(3698.1, -3987.95) * mm, "end": v(3695.67, -3981.87) * mm});
            skLineSegment(sketch, "E347", {"start": v(3695.67, -3981.87) * mm, "end": v(3694.4, -3979.04) * mm});
            skLineSegment(sketch, "E348", {"start": v(3694.4, -3979.04) * mm, "end": v(3531.83, -3654.48) * mm});
            skLineSegment(sketch, "E349", {"start": v(3531.83, -3654.48) * mm, "end": v(3907.17, -3383.75) * mm});
            skLineSegment(sketch, "E350", {"start": v(3907.17, -3383.75) * mm, "end": v(4163.85, -3640.43) * mm});
            skLineSegment(sketch, "E351", {"start": v(4163.85, -3640.43) * mm, "end": v(4166.13, -3642.52) * mm});
            skLineSegment(sketch, "E352", {"start": v(4166.13, -3642.52) * mm, "end": v(4171.14, -3646.74) * mm});
            skLineSegment(sketch, "E353", {"start": v(4171.14, -3646.74) * mm, "end": v(4179.05, -3652.85) * mm});
            skLineSegment(sketch, "E354", {"start": v(4179.05, -3652.85) * mm, "end": v(4190.04, -3660.6) * mm});
            skLineSegment(sketch, "E355", {"start": v(4190.04, -3660.6) * mm, "end": v(4204.25, -3669.73) * mm});
            skLineSegment(sketch, "E356", {"start": v(4204.25, -3669.73) * mm, "end": v(4221.82, -3679.96) * mm});
            skLineSegment(sketch, "E357", {"start": v(4221.82, -3679.96) * mm, "end": v(4242.87, -3691.02) * mm});
            skLineSegment(sketch, "E358", {"start": v(4242.87, -3691.02) * mm, "end": v(4267.5, -3702.63) * mm});
            skLineSegment(sketch, "E359", {"start": v(4267.5, -3702.63) * mm, "end": v(4295.8, -3714.48) * mm});
            skLineSegment(sketch, "E360", {"start": v(4295.8, -3714.48) * mm, "end": v(4327.82, -3726.28) * mm});
            skLineSegment(sketch, "E361", {"start": v(4327.82, -3726.28) * mm, "end": v(4363.6, -3737.72) * mm});
            skLineSegment(sketch, "E362", {"start": v(4363.6, -3737.72) * mm, "end": v(4403.18, -3748.5) * mm});
            skLineSegment(sketch, "E363", {"start": v(4403.18, -3748.5) * mm, "end": v(4446.55, -3758.3) * mm});
            skLineSegment(sketch, "E364", {"start": v(4446.55, -3758.3) * mm, "end": v(4493.7, -3766.8) * mm});
            skLineSegment(sketch, "E365", {"start": v(4493.7, -3766.8) * mm, "end": v(4544.58, -3773.72) * mm});
            skLineSegment(sketch, "E366", {"start": v(4544.58, -3773.72) * mm, "end": v(4599.15, -3778.72) * mm});
            skLineSegment(sketch, "E367", {"start": v(4599.15, -3778.72) * mm, "end": v(4657.34, -3781.5) * mm});
            skLineSegment(sketch, "E368", {"start": v(4657.34, -3781.5) * mm, "end": v(4719.03, -3781.76) * mm});
            skLineSegment(sketch, "E369", {"start": v(4719.03, -3781.76) * mm, "end": v(4784.13, -3779.2) * mm});
            skLineSegment(sketch, "E370", {"start": v(4784.13, -3779.2) * mm, "end": v(4852.48, -3773.5) * mm});
            skLineSegment(sketch, "E371", {"start": v(4852.48, -3773.5) * mm, "end": v(4923.94, -3764.4) * mm});
            skLineSegment(sketch, "E372", {"start": v(4923.94, -3764.4) * mm, "end": v(4998.33, -3751.6) * mm});
            skLineSegment(sketch, "E373", {"start": v(4998.33, -3751.6) * mm, "end": v(5035.2, -3709.6) * mm});
            skLineSegment(sketch, "E374", {"start": v(5035.2, -3709.6) * mm, "end": v(5053.8, -3679.48) * mm});
            skLineSegment(sketch, "E375", {"start": v(5053.8, -3679.48) * mm, "end": v(5074.84, -3627.7) * mm});
            skLineSegment(sketch, "E376", {"start": v(5074.84, -3627.7) * mm, "end": v(5052.97, -3555.45) * mm});
            skLineSegment(sketch, "E377", {"start": v(5052.97, -3555.45) * mm, "end": v(5029.1, -3487.48) * mm});
            skLineSegment(sketch, "E378", {"start": v(5029.1, -3487.48) * mm, "end": v(5003.58, -3423.82) * mm});
            skLineSegment(sketch, "E379", {"start": v(5003.58, -3423.82) * mm, "end": v(4976.72, -3364.47) * mm});
            skLineSegment(sketch, "E380", {"start": v(4976.72, -3364.47) * mm, "end": v(4948.86, -3309.42) * mm});
            skLineSegment(sketch, "E381", {"start": v(4948.86, -3309.42) * mm, "end": v(4920.32, -3258.65) * mm});
            skLineSegment(sketch, "E382", {"start": v(4920.32, -3258.65) * mm, "end": v(4891.4, -3212.1) * mm});
            skLineSegment(sketch, "E383", {"start": v(4891.4, -3212.1) * mm, "end": v(4862.43, -3169.69) * mm});
            skLineSegment(sketch, "E384", {"start": v(4862.43, -3169.69) * mm, "end": v(4833.7, -3131.35) * mm});
            skLineSegment(sketch, "E385", {"start": v(4833.7, -3131.35) * mm, "end": v(4805.52, -3096.96) * mm});
            skLineSegment(sketch, "E386", {"start": v(4805.52, -3096.96) * mm, "end": v(4778.16, -3066.4) * mm});
            skLineSegment(sketch, "E387", {"start": v(4778.16, -3066.4) * mm, "end": v(4751.9, -3039.53) * mm});
            skLineSegment(sketch, "E388", {"start": v(4751.9, -3039.53) * mm, "end": v(4727.01, -3016.2) * mm});
            skLineSegment(sketch, "E389", {"start": v(4727.01, -3016.2) * mm, "end": v(4703.75, -2996.2) * mm});
            skLineSegment(sketch, "E390", {"start": v(4703.75, -2996.2) * mm, "end": v(4682.34, -2979.37) * mm});
            skLineSegment(sketch, "E391", {"start": v(4682.34, -2979.37) * mm, "end": v(4663.02, -2965.5) * mm});
            skLineSegment(sketch, "E392", {"start": v(4663.02, -2965.5) * mm, "end": v(4646, -2954.37) * mm});
            skLineSegment(sketch, "E393", {"start": v(4646, -2954.37) * mm, "end": v(4631.48, -2945.76) * mm});
            skLineSegment(sketch, "E394", {"start": v(4631.48, -2945.76) * mm, "end": v(4619.63, -2939.4) * mm});
            skLineSegment(sketch, "E395", {"start": v(4619.63, -2939.4) * mm, "end": v(4610.62, -2935.07) * mm});
            skLineSegment(sketch, "E396", {"start": v(4610.62, -2935.07) * mm, "end": v(4604.6, -2932.48) * mm});
            skLineSegment(sketch, "E397", {"start": v(4604.6, -2932.48) * mm, "end": v(4601.7, -2931.38) * mm});
            skLineSegment(sketch, "E398", {"start": v(4601.7, -2931.38) * mm, "end": v(4257.25, -2816.83) * mm});
            skLineSegment(sketch, "E399", {"start": v(4257.25, -2816.83) * mm, "end": v(4331.22, -2360) * mm});
            skLineSegment(sketch, "E400", {"start": v(4331.22, -2360) * mm, "end": v(4694.22, -2360) * mm});
            skLineSegment(sketch, "E401", {"start": v(4694.22, -2360) * mm, "end": v(4697.31, -2359.85) * mm});
            skLineSegment(sketch, "E402", {"start": v(4697.31, -2359.85) * mm, "end": v(4703.84, -2359.3) * mm});
            skLineSegment(sketch, "E403", {"start": v(-2619.7, 2299.48) * mm, "end": v(-3026.1, 2299.48) * mm});
            skFitSpline(sketch, "E404", {"points": [v(-646.03, 2767.06) * mm, v(-646.03, 2714.18) * mm, v(-667.04, 2663.46) * mm, v(-704.43, 2626.07) * mm]});
            skFitSpline(sketch, "E405", {"points": [v(-704.43, 2626.07) * mm, v(-741.83, 2588.67) * mm, v(-792.54, 2567.67) * mm, v(-845.42, 2567.67) * mm]});
            skFitSpline(sketch, "E406", {"points": [v(-845.42, 2567.67) * mm, v(-898.3, 2567.67) * mm, v(-949.02, 2588.67) * mm, v(-986.41, 2626.07) * mm]});
            skFitSpline(sketch, "E407", {"points": [v(-986.41, 2626.07) * mm, v(-1023.8, 2663.46) * mm, v(-1044.81, 2714.18) * mm, v(-1044.81, 2767.06) * mm]});
            skFitSpline(sketch, "E408", {"points": [v(-1044.81, 2767.06) * mm, v(-1044.81, 2819.94) * mm, v(-1023.8, 2870.65) * mm, v(-986.41, 2908.05) * mm]});
            skFitSpline(sketch, "E409", {"points": [v(-986.41, 2908.05) * mm, v(-949.02, 2945.44) * mm, v(-898.3, 2966.45) * mm, v(-845.42, 2966.45) * mm]});
            skFitSpline(sketch, "E410", {"points": [v(-845.42, 2966.45) * mm, v(-792.54, 2966.45) * mm, v(-741.83, 2945.44) * mm, v(-704.43, 2908.05) * mm]});
            skFitSpline(sketch, "E411", {"points": [v(-704.43, 2908.05) * mm, v(-667.04, 2870.65) * mm, v(-646.03, 2819.94) * mm, v(-646.03, 2767.06) * mm]});
            skLineSegment(sketch, "E412", {"start": v(-2822.9, 2096.28) * mm, "end": v(-2822.9, 2502.68) * mm});
            skLineSegment(sketch, "E413", {"start": v(-3418.07, 3228.3) * mm, "end": v(-3446.72, 3209.2) * mm});
            skLineSegment(sketch, "E414", {"start": v(-3446.72, 3209.2) * mm, "end": v(-3474.76, 3189.3) * mm});
            skLineSegment(sketch, "E415", {"start": v(-3474.76, 3189.3) * mm, "end": v(-3502.4, 3168.57) * mm});
            skLineSegment(sketch, "E416", {"start": v(-3502.4, 3168.57) * mm, "end": v(-3529.22, 3146.82) * mm});
            skLineSegment(sketch, "E417", {"start": v(-3434.12, 3133.62) * mm, "end": v(-3515.6, 3244.97) * mm});
            skLineSegment(sketch, "E418", {"start": v(-3455.25, 3286.22) * mm, "end": v(-3466.23, 3237.65) * mm});
            skLineSegment(sketch, "E419", {"start": v(-3466.23, 3237.65) * mm, "end": v(-3474.76, 3189.3) * mm});
            skLineSegment(sketch, "E420", {"start": v(-3474.76, 3189.3) * mm, "end": v(-3481.06, 3141.34) * mm});
            skLineSegment(sketch, "E421", {"start": v(-3481.06, 3141.34) * mm, "end": v(-3484.92, 3093.79) * mm});
            skLineSegment(sketch, "E422", {"start": v(-3380.88, 3170.2) * mm, "end": v(-3427.21, 3180.76) * mm});
            skLineSegment(sketch, "E423", {"start": v(-3427.21, 3180.76) * mm, "end": v(-3474.76, 3189.3) * mm});
            skLineSegment(sketch, "E424", {"start": v(-3474.76, 3189.3) * mm, "end": v(-3523.53, 3195.6) * mm});
            skLineSegment(sketch, "E425", {"start": v(-3523.53, 3195.6) * mm, "end": v(-3573.31, 3199.86) * mm});
            skLineSegment(sketch, "E426", {"start": v(-3238.44, 3246.4) * mm, "end": v(-3253.07, 3201.9) * mm});
            skLineSegment(sketch, "E427", {"start": v(-3253.07, 3201.9) * mm, "end": v(-3281.11, 3188.07) * mm});
            skLineSegment(sketch, "E428", {"start": v(-3281.11, 3188.07) * mm, "end": v(-3325.4, 3203.31) * mm});
            skLineSegment(sketch, "E429", {"start": v(-3325.4, 3203.31) * mm, "end": v(-3392.26, 3323.81) * mm});
            skLineSegment(sketch, "E430", {"start": v(-3392.26, 3323.81) * mm, "end": v(-3375.8, 3371.77) * mm});
            skLineSegment(sketch, "E431", {"start": v(-3375.8, 3371.77) * mm, "end": v(-3342.07, 3388.63) * mm});
            skLineSegment(sketch, "E432", {"start": v(-3342.07, 3388.63) * mm, "end": v(-3293.91, 3372.78) * mm});
            skLineSegment(sketch, "E433", {"start": v(-3293.91, 3372.78) * mm, "end": v(-3238.44, 3246.4) * mm});
            skLineSegment(sketch, "E434", {"start": v(-2907.02, 3503.03) * mm, "end": v(-2892.6, 3296.79) * mm});
            skLineSegment(sketch, "E435", {"start": v(-2892.6, 3296.79) * mm, "end": v(-2928.97, 3345.55) * mm});
            skLineSegment(sketch, "E436", {"start": v(-2928.97, 3345.55) * mm, "end": v(-2968.39, 3392.9) * mm});
            skLineSegment(sketch, "E437", {"start": v(-2968.39, 3392.9) * mm, "end": v(-3010.86, 3438.82) * mm});
            skLineSegment(sketch, "E438", {"start": v(-3010.86, 3438.82) * mm, "end": v(-3056.37, 3483.12) * mm});
            skLineSegment(sketch, "E439", {"start": v(-3056.37, 3483.12) * mm, "end": v(-3016.34, 3280.33) * mm});
            skLineSegment(sketch, "E440", {"start": v(-2689.4, 3429.27) * mm, "end": v(-2724.75, 3432.73) * mm});
            skLineSegment(sketch, "E441", {"start": v(-2724.75, 3432.73) * mm, "end": v(-2760.1, 3435.37) * mm});
            skLineSegment(sketch, "E442", {"start": v(-2760.1, 3435.37) * mm, "end": v(-2795.67, 3436.79) * mm});
            skLineSegment(sketch, "E443", {"start": v(-2795.67, 3436.79) * mm, "end": v(-2831.23, 3437) * mm});
            skLineSegment(sketch, "E444", {"start": v(-2697.52, 3360.8) * mm, "end": v(-2730.64, 3364.04) * mm});
            skLineSegment(sketch, "E445", {"start": v(-2730.64, 3364.04) * mm, "end": v(-2763.97, 3366.48) * mm});
            skLineSegment(sketch, "E446", {"start": v(-2763.97, 3366.48) * mm, "end": v(-2797.3, 3367.7) * mm});
            skLineSegment(sketch, "E447", {"start": v(-2797.3, 3367.7) * mm, "end": v(-2830.82, 3368.1) * mm});
            skLineSegment(sketch, "E448", {"start": v(-2591.45, 3378.07) * mm, "end": v(-2631.48, 3350.84) * mm});
            skLineSegment(sketch, "E449", {"start": v(-2631.48, 3350.84) * mm, "end": v(-2637.58, 3316.9) * mm});
            skLineSegment(sketch, "E450", {"start": v(-2637.58, 3316.9) * mm, "end": v(-2613.2, 3276.87) * mm});
            skLineSegment(sketch, "E451", {"start": v(-2613.2, 3276.87) * mm, "end": v(-2582.71, 3269.76) * mm});
            skLineSegment(sketch, "E452", {"start": v(-2582.71, 3269.76) * mm, "end": v(-2552.44, 3261.83) * mm});
            skLineSegment(sketch, "E453", {"start": v(-2552.44, 3261.83) * mm, "end": v(-2512.2, 3285.81) * mm});
            skLineSegment(sketch, "E454", {"start": v(-2512.2, 3285.81) * mm, "end": v(-2501.84, 3318.73) * mm});
            skLineSegment(sketch, "E455", {"start": v(-2501.84, 3318.73) * mm, "end": v(-2524.6, 3361.4) * mm});
            skLineSegment(sketch, "E456", {"start": v(-2524.6, 3361.4) * mm, "end": v(-2557.92, 3370.34) * mm});
            skLineSegment(sketch, "E457", {"start": v(-2557.92, 3370.34) * mm, "end": v(-2591.45, 3378.07) * mm});
            skLineSegment(sketch, "E458", {"start": v(-2591.45, 3378.07) * mm, "end": v(-2619.09, 3418.7) * mm});
            skLineSegment(sketch, "E459", {"start": v(-2619.09, 3418.7) * mm, "end": v(-2612.79, 3452.44) * mm});
            skLineSegment(sketch, "E460", {"start": v(-2612.79, 3452.44) * mm, "end": v(-2569.7, 3479.06) * mm});
            skLineSegment(sketch, "E461", {"start": v(-2569.7, 3479.06) * mm, "end": v(-2532.93, 3470.72) * mm});
            skLineSegment(sketch, "E462", {"start": v(-2532.93, 3470.72) * mm, "end": v(-2496.56, 3460.97) * mm});
            skLineSegment(sketch, "E463", {"start": v(-2496.56, 3460.97) * mm, "end": v(-2470.75, 3417.28) * mm});
            skLineSegment(sketch, "E464", {"start": v(-2470.75, 3417.28) * mm, "end": v(-2481.11, 3384.57) * mm});
            skLineSegment(sketch, "E465", {"start": v(-2481.11, 3384.57) * mm, "end": v(-2524.6, 3361.4) * mm});
            skLineSegment(sketch, "E466", {"start": v(-2271, 3254.52) * mm, "end": v(-2241.54, 3236.84) * mm});
            skLineSegment(sketch, "E467", {"start": v(-2241.54, 3236.84) * mm, "end": v(-2212.48, 3218.35) * mm});
            skLineSegment(sketch, "E468", {"start": v(-2212.48, 3218.35) * mm, "end": v(-2184.04, 3198.84) * mm});
            skLineSegment(sketch, "E469", {"start": v(-2184.04, 3198.84) * mm, "end": v(-2135.47, 3205.75) * mm});
            skLineSegment(sketch, "E470", {"start": v(-2135.47, 3205.75) * mm, "end": v(-2114.54, 3233.18) * mm});
            skLineSegment(sketch, "E471", {"start": v(-2114.54, 3233.18) * mm, "end": v(-2124.1, 3282.97) * mm});
            skLineSegment(sketch, "E472", {"start": v(-2124.1, 3282.97) * mm, "end": v(-2155.18, 3304.5) * mm});
            skLineSegment(sketch, "E473", {"start": v(-2155.18, 3304.5) * mm, "end": v(-2186.88, 3324.83) * mm});
            skLineSegment(sketch, "E474", {"start": v(-2186.88, 3324.83) * mm, "end": v(-2219.4, 3344.13) * mm});
            skLineSegment(sketch, "E475", {"start": v(-2219.4, 3344.13) * mm, "end": v(-2322.82, 3165.11) * mm});
            skLineSegment(sketch, "E476", {"start": v(-2170.22, 3056.6) * mm, "end": v(-2080.2, 3161.05) * mm});
            skLineSegment(sketch, "E477", {"start": v(-2057.64, 3187.26) * mm, "end": v(-2035.09, 3213.27) * mm});
            skLineSegment(sketch, "E478", {"start": v(-2013.55, 2943.22) * mm, "end": v(-2060.29, 2945.86) * mm});
            skLineSegment(sketch, "E479", {"start": v(-2060.29, 2945.86) * mm, "end": v(-2055.2, 2992.4) * mm});
            skLineSegment(sketch, "E480", {"start": v(-2055.2, 2992.4) * mm, "end": v(-1927.4, 3108.01) * mm});
            skLineSegment(sketch, "E481", {"start": v(-1932.68, 3007.63) * mm, "end": v(-1955.23, 3035.06) * mm});
            skLineSegment(sketch, "E482", {"start": v(-1955.23, 3035.06) * mm, "end": v(-1978.6, 3061.68) * mm});
            skLineSegment(sketch, "E483", {"start": v(-1978.6, 3061.68) * mm, "end": v(-2002.78, 3087.7) * mm});
            skLineSegment(sketch, "E484", {"start": v(-2002.78, 3087.7) * mm, "end": v(-2027.77, 3113.1) * mm});
            skLineSegment(sketch, "E485", {"start": v(-1938.16, 2765.01) * mm, "end": v(-1953.2, 2792.44) * mm});
            skLineSegment(sketch, "E486", {"start": v(-1953.2, 2792.44) * mm, "end": v(-1969.05, 2819.27) * mm});
            skLineSegment(sketch, "E487", {"start": v(-1969.05, 2819.27) * mm, "end": v(-1985.71, 2845.68) * mm});
            skLineSegment(sketch, "E488", {"start": v(-1985.71, 2845.68) * mm, "end": v(-1974.94, 2891.4) * mm});
            skLineSegment(sketch, "E489", {"start": v(-1974.94, 2891.4) * mm, "end": v(-1918.45, 2930.82) * mm});
            skLineSegment(sketch, "E490", {"start": v(-1918.45, 2930.82) * mm, "end": v(-1870.3, 2921.07) * mm});
            skLineSegment(sketch, "E491", {"start": v(-1870.3, 2921.07) * mm, "end": v(-1851.2, 2891) * mm});
            skLineSegment(sketch, "E492", {"start": v(-1851.2, 2891) * mm, "end": v(-1833.31, 2860.31) * mm});
            skLineSegment(sketch, "E493", {"start": v(-1833.31, 2860.31) * mm, "end": v(-1816.24, 2829.22) * mm});
            skLineSegment(sketch, "E494", {"start": v(-1847.94, 2736.97) * mm, "end": v(-1802.83, 2719.5) * mm});
            skLineSegment(sketch, "E495", {"start": v(-1802.83, 2719.5) * mm, "end": v(-1757.92, 2699.58) * mm});
            skLineSegment(sketch, "E496", {"start": v(-1757.92, 2699.58) * mm, "end": v(-1745.94, 2666.05) * mm});
            skLineSegment(sketch, "E497", {"start": v(-1745.94, 2666.05) * mm, "end": v(-1768.08, 2622.16) * mm});
            skLineSegment(sketch, "E498", {"start": v(-1768.08, 2622.16) * mm, "end": v(-1867.04, 2591.88) * mm});
            skLineSegment(sketch, "E499", {"start": v(-1910.93, 2708.72) * mm, "end": v(-1722.16, 2793.46) * mm});
            skLineSegment(sketch, "E500", {"start": v(-1826.2, 2377.5) * mm, "end": v(-1824.37, 2346.42) * mm});
            skLineSegment(sketch, "E501", {"start": v(-1824.37, 2346.42) * mm, "end": v(-1823.36, 2315.13) * mm});
            skLineSegment(sketch, "E502", {"start": v(-1823.36, 2315.13) * mm, "end": v(-1823.36, 2283.83) * mm});
            skLineSegment(sketch, "E503", {"start": v(-1823.36, 2283.83) * mm, "end": v(-1789.83, 2251.12) * mm});
            skLineSegment(sketch, "E504", {"start": v(-1789.83, 2251.12) * mm, "end": v(-1652.06, 2244.62) * mm});
            skLineSegment(sketch, "E505", {"start": v(-1652.06, 2244.62) * mm, "end": v(-1616.5, 2280.58) * mm});
            skLineSegment(sketch, "E506", {"start": v(-1616.5, 2280.58) * mm, "end": v(-1616.5, 2318.38) * mm});
            skLineSegment(sketch, "E507", {"start": v(-1616.5, 2318.38) * mm, "end": v(-1617.72, 2355.97) * mm});
            skLineSegment(sketch, "E508", {"start": v(-1617.72, 2355.97) * mm, "end": v(-1620.16, 2393.56) * mm});
            skLineSegment(sketch, "E509", {"start": v(-1617.72, 2355.97) * mm, "end": v(-1824.37, 2346.42) * mm});
            skLineSegment(sketch, "E510", {"start": v(-1716.47, 2035.32) * mm, "end": v(-1708.75, 2070.07) * mm});
            skLineSegment(sketch, "E511", {"start": v(-1708.75, 2070.07) * mm, "end": v(-1702.04, 2105.02) * mm});
            skLineSegment(sketch, "E512", {"start": v(-1702.04, 2105.02) * mm, "end": v(-1696.56, 2139.97) * mm});
            skLineSegment(sketch, "E513", {"start": v(-1696.56, 2139.97) * mm, "end": v(-1692.09, 2175.32) * mm});
            skLineSegment(sketch, "E514", {"start": v(-1783.53, 2051.37) * mm, "end": v(-1776.21, 2083.88) * mm});
            skLineSegment(sketch, "E515", {"start": v(-1776.21, 2083.88) * mm, "end": v(-1770.12, 2116.8) * mm});
            skLineSegment(sketch, "E516", {"start": v(-1770.12, 2116.8) * mm, "end": v(-1764.83, 2149.72) * mm});
            skLineSegment(sketch, "E517", {"start": v(-1764.83, 2149.72) * mm, "end": v(-1760.57, 2182.84) * mm});
            skLineSegment(sketch, "E518", {"start": v(-1910.93, 1890.23) * mm, "end": v(-1898.54, 1918.89) * mm});
            skLineSegment(sketch, "E519", {"start": v(-1898.54, 1918.89) * mm, "end": v(-1887.16, 1947.94) * mm});
            skLineSegment(sketch, "E520", {"start": v(-1887.16, 1947.94) * mm, "end": v(-1876.6, 1977.4) * mm});
            skLineSegment(sketch, "E521", {"start": v(-1876.6, 1977.4) * mm, "end": v(-1867.04, 2007.07) * mm});
            skLineSegment(sketch, "E522", {"start": v(-1867.04, 2007.07) * mm, "end": v(-1801, 1986.96) * mm});
            skLineSegment(sketch, "E523", {"start": v(-1801, 1986.96) * mm, "end": v(-1778.65, 1944.08) * mm});
            skLineSegment(sketch, "E524", {"start": v(-1778.65, 1944.08) * mm, "end": v(-1790.23, 1911.57) * mm});
            skLineSegment(sketch, "E525", {"start": v(-1790.23, 1911.57) * mm, "end": v(-1802.83, 1879.47) * mm});
            skLineSegment(sketch, "E526", {"start": v(-1802.83, 1879.47) * mm, "end": v(-1785.15, 1833.75) * mm});
            skLineSegment(sketch, "E527", {"start": v(-1785.15, 1833.75) * mm, "end": v(-1753.66, 1819.52) * mm});
            skLineSegment(sketch, "E528", {"start": v(-1753.66, 1819.52) * mm, "end": v(-1707.33, 1840.04) * mm});
            skLineSegment(sketch, "E529", {"start": v(-1707.33, 1840.04) * mm, "end": v(-1693.51, 1875.2) * mm});
            skLineSegment(sketch, "E530", {"start": v(-1693.51, 1875.2) * mm, "end": v(-1680.7, 1910.76) * mm});
            skLineSegment(sketch, "E531", {"start": v(-1680.7, 1910.76) * mm, "end": v(-1702.04, 1956.68) * mm});
            skLineSegment(sketch, "E532", {"start": v(-1938.57, 1640.1) * mm, "end": v(-1959.5, 1612.87) * mm});
            skLineSegment(sketch, "E533", {"start": v(-1959.5, 1612.87) * mm, "end": v(-1981.44, 1586.25) * mm});
            skLineSegment(sketch, "E534", {"start": v(-1981.44, 1586.25) * mm, "end": v(-2004.2, 1560.24) * mm});
            skLineSegment(sketch, "E535", {"start": v(-2004.2, 1560.24) * mm, "end": v(-2002.78, 1511.27) * mm});
            skLineSegment(sketch, "E536", {"start": v(-2002.78, 1511.27) * mm, "end": v(-1978, 1487.29) * mm});
            skLineSegment(sketch, "E537", {"start": v(-1978, 1487.29) * mm, "end": v(-1927.4, 1490.95) * mm});
            skLineSegment(sketch, "E538", {"start": v(-1927.4, 1490.95) * mm, "end": v(-1902.6, 1519.4) * mm});
            skLineSegment(sketch, "E539", {"start": v(-1902.6, 1519.4) * mm, "end": v(-1878.63, 1548.45) * mm});
            skLineSegment(sketch, "E540", {"start": v(-1878.63, 1548.45) * mm, "end": v(-1855.66, 1578.32) * mm});
            skLineSegment(sketch, "E541", {"start": v(-1855.66, 1578.32) * mm, "end": v(-2021.48, 1702.07) * mm});
            skLineSegment(sketch, "E542", {"start": v(-2164.12, 1372.07) * mm, "end": v(-2135.47, 1393.2) * mm});
            skLineSegment(sketch, "E543", {"start": v(-2135.47, 1393.2) * mm, "end": v(-2107.43, 1415.15) * mm});
            skLineSegment(sketch, "E544", {"start": v(-2107.43, 1415.15) * mm, "end": v(-2080.2, 1437.91) * mm});
            skLineSegment(sketch, "E545", {"start": v(-2080.2, 1437.91) * mm, "end": v(-2053.58, 1461.48) * mm});
            skLineSegment(sketch, "E546", {"start": v(-2203.95, 1428.36) * mm, "end": v(-2177.13, 1448.07) * mm});
            skLineSegment(sketch, "E547", {"start": v(-2177.13, 1448.07) * mm, "end": v(-2150.91, 1468.6) * mm});
            skLineSegment(sketch, "E548", {"start": v(-2150.91, 1468.6) * mm, "end": v(-2125.1, 1490.13) * mm});
            skLineSegment(sketch, "E549", {"start": v(-2125.1, 1490.13) * mm, "end": v(-2100.32, 1512.28) * mm});
            skLineSegment(sketch, "E550", {"start": v(-2377.28, 1328.18) * mm, "end": v(-2347.2, 1342.61) * mm});
            skLineSegment(sketch, "E551", {"start": v(-2347.2, 1342.61) * mm, "end": v(-2317.54, 1358.05) * mm});
            skLineSegment(sketch, "E552", {"start": v(-2317.54, 1358.05) * mm, "end": v(-2288.28, 1374.1) * mm});
            skLineSegment(sketch, "E553", {"start": v(-2288.28, 1374.1) * mm, "end": v(-2259.63, 1391.38) * mm});
            skLineSegment(sketch, "E554", {"start": v(-2259.63, 1391.38) * mm, "end": v(-2265.32, 1334.48) * mm});
            skLineSegment(sketch, "E555", {"start": v(-2265.32, 1334.48) * mm, "end": v(-2274.05, 1276.98) * mm});
            skLineSegment(sketch, "E556", {"start": v(-2274.05, 1276.98) * mm, "end": v(-2285.64, 1219.07) * mm});
            skLineSegment(sketch, "E557", {"start": v(-2285.64, 1219.07) * mm, "end": v(-2377.89, 1404.38) * mm});
            skLineSegment(sketch, "E558", {"start": v(-2591.45, 1220.9) * mm, "end": v(-2625.18, 1214.19) * mm});
            skLineSegment(sketch, "E559", {"start": v(-2625.18, 1214.19) * mm, "end": v(-2659.32, 1208.7) * mm});
            skLineSegment(sketch, "E560", {"start": v(-2659.32, 1208.7) * mm, "end": v(-2693.46, 1204.03) * mm});
            skLineSegment(sketch, "E561", {"start": v(-2693.46, 1204.03) * mm, "end": v(-2724.75, 1166.23) * mm});
            skLineSegment(sketch, "E562", {"start": v(-2724.75, 1166.23) * mm, "end": v(-2721.7, 1131.9) * mm});
            skLineSegment(sketch, "E563", {"start": v(-2721.7, 1131.9) * mm, "end": v(-2681.27, 1101.41) * mm});
            skLineSegment(sketch, "E564", {"start": v(-2681.27, 1101.41) * mm, "end": v(-2643.88, 1106.29) * mm});
            skLineSegment(sketch, "E565", {"start": v(-2643.88, 1106.29) * mm, "end": v(-2606.7, 1112.59) * mm});
            skLineSegment(sketch, "E566", {"start": v(-2606.7, 1112.59) * mm, "end": v(-2569.7, 1119.9) * mm});
            skLineSegment(sketch, "E567", {"start": v(-2569.7, 1119.9) * mm, "end": v(-2613.2, 1322.09) * mm});
            skLineSegment(sketch, "E568", {"start": v(-2798.92, 1300.14) * mm, "end": v(-2797.3, 1231.26) * mm});
            skLineSegment(sketch, "E569", {"start": v(-2797.3, 1231.26) * mm, "end": v(-2831.23, 1161.97) * mm});
            skLineSegment(sketch, "E570", {"start": v(-2831.23, 1161.97) * mm, "end": v(-2869.43, 1093.9) * mm});
            skLineSegment(sketch, "E571", {"start": v(-2869.43, 1093.9) * mm, "end": v(-2902.35, 1164.6) * mm});
            skLineSegment(sketch, "E572", {"start": v(-2902.35, 1164.6) * mm, "end": v(-2930.8, 1236.34) * mm});
            skLineSegment(sketch, "E573", {"start": v(-2930.8, 1236.34) * mm, "end": v(-2923.68, 1304.82) * mm});
            skLineSegment(sketch, "E574", {"start": v(-2797.3, 1231.26) * mm, "end": v(-2830.82, 1230.85) * mm});
            skLineSegment(sketch, "E575", {"start": v(-2830.82, 1230.85) * mm, "end": v(-2864.15, 1231.66) * mm});
            skLineSegment(sketch, "E576", {"start": v(-2864.15, 1231.66) * mm, "end": v(-2897.47, 1233.5) * mm});
            skLineSegment(sketch, "E577", {"start": v(-2897.47, 1233.5) * mm, "end": v(-2930.8, 1236.34) * mm});
            skLineSegment(sketch, "E578", {"start": v(-3146.6, 1208.9) * mm, "end": v(-3112.46, 1199.35) * mm});
            skLineSegment(sketch, "E579", {"start": v(-3112.46, 1199.35) * mm, "end": v(-3077.91, 1190.82) * mm});
            skLineSegment(sketch, "E580", {"start": v(-3077.91, 1190.82) * mm, "end": v(-3043.16, 1183.5) * mm});
            skLineSegment(sketch, "E581", {"start": v(-3043.16, 1183.5) * mm, "end": v(-3008.21, 1177.2) * mm});
            skLineSegment(sketch, "E582", {"start": v(-3127.09, 1275.15) * mm, "end": v(-3094.78, 1266) * mm});
            skLineSegment(sketch, "E583", {"start": v(-3094.78, 1266) * mm, "end": v(-3062.47, 1258.08) * mm});
            skLineSegment(sketch, "E584", {"start": v(-3062.47, 1258.08) * mm, "end": v(-3029.75, 1251.17) * mm});
            skLineSegment(sketch, "E585", {"start": v(-3029.75, 1251.17) * mm, "end": v(-2996.84, 1245.07) * mm});
            skLineSegment(sketch, "E586", {"start": v(-3281.11, 1410.89) * mm, "end": v(-3253.07, 1397.07) * mm});
            skLineSegment(sketch, "E587", {"start": v(-3253.07, 1397.07) * mm, "end": v(-3224.62, 1384.06) * mm});
            skLineSegment(sketch, "E588", {"start": v(-3224.62, 1384.06) * mm, "end": v(-3195.77, 1372.07) * mm});
            skLineSegment(sketch, "E589", {"start": v(-3195.77, 1372.07) * mm, "end": v(-3166.71, 1360.7) * mm});
            skLineSegment(sketch, "E590", {"start": v(-3166.71, 1360.7) * mm, "end": v(-3190.48, 1296.08) * mm});
            skLineSegment(sketch, "E591", {"start": v(-3190.48, 1296.08) * mm, "end": v(-3234.38, 1275.96) * mm});
            skLineSegment(sketch, "E592", {"start": v(-3234.38, 1275.96) * mm, "end": v(-3266.28, 1289.37) * mm});
            skLineSegment(sketch, "E593", {"start": v(-3266.28, 1289.37) * mm, "end": v(-3297.57, 1303.8) * mm});
            skLineSegment(sketch, "E594", {"start": v(-3297.57, 1303.8) * mm, "end": v(-3344.3, 1288.36) * mm});
            skLineSegment(sketch, "E595", {"start": v(-3344.3, 1288.36) * mm, "end": v(-3359.95, 1257.88) * mm});
            skLineSegment(sketch, "E596", {"start": v(-3359.95, 1257.88) * mm, "end": v(-3342.07, 1210.33) * mm});
            skLineSegment(sketch, "E597", {"start": v(-3342.07, 1210.33) * mm, "end": v(-3307.73, 1194.68) * mm});
            skLineSegment(sketch, "E598", {"start": v(-3307.73, 1194.68) * mm, "end": v(-3272.98, 1180.05) * mm});
            skLineSegment(sketch, "E599", {"start": v(-3272.98, 1180.05) * mm, "end": v(-3226.04, 1198.95) * mm});
            skFitSpline(sketch, "E600", {"points": [v(-790.9, 2299.48) * mm, v(-790.9, 1760.56) * mm, v(-1004.98, 1243.71) * mm, v(-1386.06, 862.64) * mm]});
            skFitSpline(sketch, "E601", {"points": [v(-1386.06, 862.64) * mm, v(-1767.13, 481.56) * mm, v(-2283.98, 267.48) * mm, v(-2822.9, 267.48) * mm]});
            skFitSpline(sketch, "E602", {"points": [v(-2822.9, 267.48) * mm, v(-3361.82, 267.48) * mm, v(-3878.66, 481.56) * mm, v(-4259.74, 862.64) * mm]});
            skFitSpline(sketch, "E603", {"points": [v(-4259.74, 862.64) * mm, v(-4640.81, 1243.71) * mm, v(-4854.9, 1760.56) * mm, v(-4854.9, 2299.48) * mm]});
            skFitSpline(sketch, "E604", {"points": [v(-4854.9, 2299.48) * mm, v(-4854.9, 2838.4) * mm, v(-4640.81, 3355.25) * mm, v(-4259.74, 3736.32) * mm]});
            skFitSpline(sketch, "E605", {"points": [v(-4259.74, 3736.32) * mm, v(-3878.66, 4117.4) * mm, v(-3361.82, 4331.48) * mm, v(-2822.9, 4331.48) * mm]});
            skFitSpline(sketch, "E606", {"points": [v(-2822.9, 4331.48) * mm, v(-2283.98, 4331.48) * mm, v(-1767.13, 4117.4) * mm, v(-1386.06, 3736.32) * mm]});
            skFitSpline(sketch, "E607", {"points": [v(-1386.06, 3736.32) * mm, v(-1004.98, 3355.25) * mm, v(-790.9, 2838.4) * mm, v(-790.9, 2299.48) * mm]});
            skLineSegment(sketch, "E608", {"start": v(-3441.64, 1263.77) * mm, "end": v(-3473.75, 1283.68) * mm});
            skLineSegment(sketch, "E609", {"start": v(-3473.75, 1283.68) * mm, "end": v(-3505.24, 1304.4) * mm});
            skLineSegment(sketch, "E610", {"start": v(-3505.24, 1304.4) * mm, "end": v(-3535.92, 1326.15) * mm});
            skLineSegment(sketch, "E611", {"start": v(-3535.92, 1326.15) * mm, "end": v(-3566, 1348.9) * mm});
            skLineSegment(sketch, "E612", {"start": v(-3566, 1348.9) * mm, "end": v(-3474.76, 1409.67) * mm});
            skLineSegment(sketch, "E613", {"start": v(-3474.76, 1409.67) * mm, "end": v(-3388.2, 1475.1) * mm});
            skFitSpline(sketch, "E614", {"points": [v(-282.9, 2299.48) * mm, v(-282.9, 1625.83) * mm, v(-550.5, 979.77) * mm, v(-1026.84, 503.43) * mm]});
            skFitSpline(sketch, "E615", {"points": [v(-1026.84, 503.43) * mm, v(-1503.19, 27.09) * mm, v(-2149.25, -240.52) * mm, v(-2822.9, -240.52) * mm]});
            skFitSpline(sketch, "E616", {"points": [v(-2822.9, -240.52) * mm, v(-3496.55, -240.52) * mm, v(-4142.6, 27.09) * mm, v(-4618.95, 503.43) * mm]});
            skFitSpline(sketch, "E617", {"points": [v(-4618.95, 503.43) * mm, v(-5095.29, 979.77) * mm, v(-5362.9, 1625.83) * mm, v(-5362.9, 2299.48) * mm]});
            skFitSpline(sketch, "E618", {"points": [v(-5362.9, 2299.48) * mm, v(-5362.9, 2973.13) * mm, v(-5095.29, 3619.19) * mm, v(-4618.95, 4095.53) * mm]});
            skFitSpline(sketch, "E619", {"points": [v(-4618.95, 4095.53) * mm, v(-4142.6, 4571.87) * mm, v(-3496.55, 4839.48) * mm, v(-2822.9, 4839.48) * mm]});
            skFitSpline(sketch, "E620", {"points": [v(-2822.9, 4839.48) * mm, v(-2149.25, 4839.48) * mm, v(-1503.19, 4571.87) * mm, v(-1026.84, 4095.53) * mm]});
            skFitSpline(sketch, "E621", {"points": [v(-1026.84, 4095.53) * mm, v(-550.5, 3619.19) * mm, v(-282.9, 2973.13) * mm, v(-282.9, 2299.48) * mm]});
            skFitSpline(sketch, "E622", {"points": [v(-1012.38, 2299.48) * mm, v(-1012.38, 1819.3) * mm, v(-1203.13, 1358.8) * mm, v(-1542.67, 1019.25) * mm]});
            skFitSpline(sketch, "E623", {"points": [v(-1542.67, 1019.25) * mm, v(-1882.2, 679.72) * mm, v(-2342.72, 488.97) * mm, v(-2822.9, 488.97) * mm]});
            skFitSpline(sketch, "E624", {"points": [v(-2822.9, 488.97) * mm, v(-3303.07, 488.97) * mm, v(-3763.58, 679.72) * mm, v(-4103.12, 1019.25) * mm]});
            skFitSpline(sketch, "E625", {"points": [v(-4103.12, 1019.25) * mm, v(-4442.66, 1358.8) * mm, v(-4633.4, 1819.3) * mm, v(-4633.4, 2299.48) * mm]});
            skFitSpline(sketch, "E626", {"points": [v(-4633.4, 2299.48) * mm, v(-4633.4, 2779.66) * mm, v(-4442.66, 3240.17) * mm, v(-4103.12, 3579.7) * mm]});
            skFitSpline(sketch, "E627", {"points": [v(-4103.12, 3579.7) * mm, v(-3763.58, 3919.24) * mm, v(-3303.07, 4110) * mm, v(-2822.9, 4110) * mm]});
            skFitSpline(sketch, "E628", {"points": [v(-2822.9, 4110) * mm, v(-2342.72, 4110) * mm, v(-1882.2, 3919.24) * mm, v(-1542.67, 3579.7) * mm]});
            skFitSpline(sketch, "E629", {"points": [v(-1542.67, 3579.7) * mm, v(-1203.13, 3240.17) * mm, v(-1012.38, 2779.66) * mm, v(-1012.38, 2299.48) * mm]});
            skSolve(sketch);
        }
        {
            var Q0;
            Q0=makeQuery(id+"F5.imprint","IMPRINT",FACE,{"disambiguationData":[TD([[makeQuery(id+"F5.imprint","IMPRINT",EDGE,{"derivedFrom":sQuery(id+"F5.wireOp",EDGE,"E3")}),1.0]])]});
            extrude(context, id + "F6", {"entities" : qUnion([Q0]), "depth" : 254 * mm});
        }
    });
